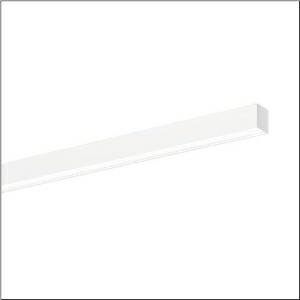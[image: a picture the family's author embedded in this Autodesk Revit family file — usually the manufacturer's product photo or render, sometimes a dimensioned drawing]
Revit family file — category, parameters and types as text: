
# Revit family: silica_r__21_51mx20tat2w_a418
name_source: partatom
category: Lighting Fixtures
units: mm (PartAtom-declared; Revit-internal decimal feet)

## family parameters
Cut with Voids When Loaded = No
Host = Face
Light Source = No
Part Type = Normal
Room Calculation Point = No
Round Connector Dimension = Use Diameter
Shared = No

## types (1)
- --- (1 x LED, 2400 lm, 20.5 W, 6500K)
    Apparent Load = 21 VA
    CIE Flux Codes = 48 79 96 100 100
    Color Rendering = 80
    Color Temperature = 6500K
    Default Elevation = 1800 mm
    Description = Silica® 21, office luminaire, primary optical cover: cover, of PMMA, opal, light emission: direct distribution, primary light characteristic: symmetric, installation type: surface-mounted, LED, rated luminous flux: 2.400lm, luminous efficacy: 112lm/W, light colour: 8tw, colour temperature: 2700..6500K, control gear: DALI DT8, with terminal, 3+2-pole, max. 2.5mm², mains connection: 220..240V, AC, 50/60Hz, rated input power: 21.5W, luminaire housing, of aluminium, traffic white (RAL 9016), length: 1.204mm, width: 53mm, height: 53mm, protection rating (complete): IP20, insulation class (complete): insulation class I (protective earthing), certification: CE, permissible operating ambient temperature: 0..+35°C, standard: EN 50419, packaging unit: 1 piece
    Height = 53 mm
    Lamp = 1 x LED
    Lamp Light Flux = 2400 lm
    Lamp Power = 20.5 W
    Lamp count = 1
    Length = 1204 mm
    Luminous efficacy = 117 lm/W
    Manufacturer = Siteco
    ModVariant = No
    Model = 51MX20TAT2W
    Mounting Place = Ceiling
    Mounting Type = Surface mounted
    Number of Poles = 1
    OnlyDefault = Yes
    Power Factor = 1
    Product Name = Silica® 21
    Product group = office luminaire | ceiling mounted
    ProductGroupID = 302
    Protection Class = Protection class I
    Protection Degree = IP 20
    RLX_Detail_Level = 1
    RLX_Emergency_Light_Flux = 0 lm
    RLX_Emergency_Type = 0
    RLX_Emergency_Type_DB = No
    RlxData = <blob elided: 20649 chars, md5=64d4b125>
    Socket = socket
    Standby Power = 0 W
    System Light Flux = 2400 lm
    System Power = 21 W
    Type Comments = individual setting
    Type Image = l_1335877.jpg
    URL = http://relux.com
    VarID = @adj_139710
    Voltage = 0 V
    Weight = 0.00 kg
    Width = 53 mm

## geometry (parser evidence)
native form markers: Blend x4, Sweep x11
no freeform markers — native parametric forms only
